# Revit family: PRD_FrankeWS_WlHngWshBsns_HEAVY-DUTY_HDTX450
name_source: partatom
category: Plumbing Fixtures
revit_build: Autodesk Revit 2018 (Build: 20190510_1515(x64)
units: mm (PartAtom-declared; Revit-internal decimal feet)

## family parameters
Cut with Voids When Loaded = Yes
Host = Face
OmniClass Number = 23.45.05.14.14
OmniClass Title = Sinks/Lavatories
Part Type = Normal
Room Calculation Point = No
Round Connector Dimension = Use Diameter
Shared = No

## types (1)
- HDTX450
    AssetType = Fixed
    BIMObjectName = PRD_AR_WallHungWashBasins_HeavyDutyWashBasin_HDTX450
    Category = Pr_40_20_96_96, Wall-hung wash basins
    Color = Stainless steel
    Default Elevation = 850 mm  [stored 2.78871 ft]
    Description = Single wash basin for wall mounting, stainless steel, surface satin finished, material thickness 1.2 mm, with 3 threaded rods for mounting through the wall via a service room, seamless welded bowl, 40 mm tap ledge, without taphole, without overflow, 1 1/4" flat perforated waste, incl. hidden mounted siphon DN 32. CE Certified
    DrainSize = 32  [stored 0.104987 ft]
    DurationUnit = year
    Features = Single washbasin, stainless steel, 1.20 mm, satin finished, bolt fix with duct wall, 450x280x400 mm (WxHxD)
    Finish = Satin finished
    Form = Wall hung wash basin
    GrossWeight = 9.30 kg
    IfcExportAs = IfcSanitaryTerminalType
    IfcExportType = WASHHANDBASIN
    IntegralAccessories = Including mounting material
    Manufacturer = KWC Group AG
    ManufacturerName = KWC Group AG
    ManufacturerURL = www.kwc.com
    Material = Stainless steel
    MaterialsBody = Stainless steel
    MaterialsFinishAndColour = Stainless steel
    Model = HDTX450
    ModelNumber = 2000100349
    ModelReference = HDTX450
    NBSDescription = Wall hung wash basins
    NBSReference = 45-35-70/369
    Name = HEAVY-DUTY Wash basins HDTX450
    NetWeight = 8.90 kg
    NominalDepth = 280 mm  [stored 0.918635 ft]
    NominalHeight = 280 mm  [stored 0.918635 ft]
    NominalLength = 400 mm  [stored 1.31234 ft]
    NominalWidth = 450 mm  [stored 1.47638 ft]
    ProductInformation = https://pim.kwc.com
    Size = 450 x 280 x 400 mm
    URL = www.kwc.com
    Uniclass2015Code = Pr_40_20_96_96
    Uniclass2015Title = Wall-hung wash basins
    Uniclass2015Version = Products v1.7
    Version = 1
    WarrantyDurationUnit = year
    WashHandBasinMounting = WallHung
    WashHandBasinType = HandRinse
    WashbasinMaterial = PRD_AR_StainlessSteel_SatinFinished
    WasteSize = 32  [stored 0.104987 ft]
    WaterSupplyOverflowAndWasteHolesOverflow = None
    WaterSupplyOverflowAndWasteHolesWaste = CENTER-BACK
    WaterSupplyOverflowAndWasteHolesWaterSupply = No tapholes

note: [stored X ft] marks values corroborated as IEEE doubles in the binary element streams (Revit-internal decimal feet)

## geometry (parser evidence)
native form markers: Sweep x2
no freeform markers — native parametric forms only
